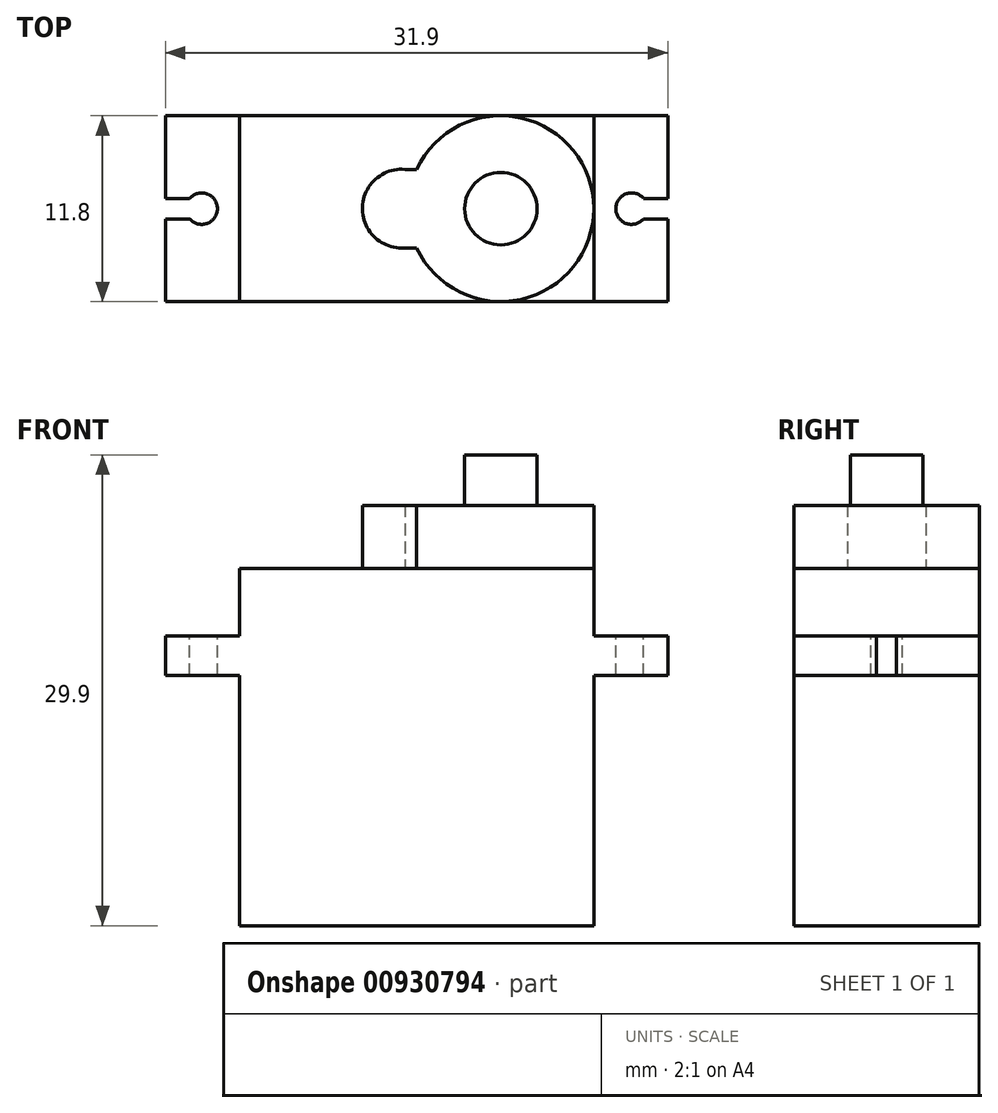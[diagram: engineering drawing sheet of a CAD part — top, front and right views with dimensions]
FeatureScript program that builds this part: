
annotation { "Feature Type Name" : "Feature", "Feature Type Description" : "" }
export const myFeature = defineFeature(function(context is Context, id is Id, definition is map)
    precondition{}
    {
        {
            var Q0;
            Q0=qCreatedBy(makeId("Top.planeOp"),FACE);
            var sketch = newSketch(context, id + "F0", { "sketchPlane" : qUnion([Q0])});
            skLineSegment(sketch, "E0.bottom", {"start": v(11.25, -5.9) * mm, "end": v(-11.25, -5.9) * mm});
            skLineSegment(sketch, "E0.top", {"start": v(11.25, 5.9) * mm, "end": v(-11.25, 5.9) * mm});
            skLineSegment(sketch, "E0.left", {"start": v(11.25, -5.9) * mm, "end": v(11.25, 5.9) * mm});
            skLineSegment(sketch, "E0.right", {"start": v(-11.25, -5.9) * mm, "end": v(-11.25, 5.9) * mm});
            skPoint(sketch, "E0.middle", {"position": v(0, 0) * mm});
            skSolve(sketch);
        }
        {
            var Q0;
            Q0=makeQuery(id+"F0.imprint","IMPRINT",FACE,{"disambiguationData":[TD([[makeQuery(id+"F0.imprint","IMPRINT",EDGE,{"derivedFrom":sQuery(id+"F0.wireOp",EDGE,"E0.bottom")}),-1.0]])]});
            extrude(context, id + "F1", {"entities" : qUnion([Q0]), "depth" : 22.7 * mm, "offsetDistance" : 25 * mm});
        }
        {
            var Q0;
            Q0=makeQuery(id+"F1.opExtrude","SWEPT_FACE",FACE,{"disambiguationData":[OSD([sQuery(id+"F0.wireOp",EDGE,"E0.right")])]});
            var sketch = newSketch(context, id + "F2", { "sketchPlane" : qUnion([Q0])});
            skLineSegment(sketch, "E1", {"start": v(-5.9, 15.9) * mm, "end": v(5.9, 15.9) * mm});
            skLineSegment(sketch, "E2", {"start": v(-5.9, 18.4) * mm, "end": v(5.9, 18.4) * mm});
            skSolve(sketch);
        }
        {
            var Q0;
            Q0 = qSketchRegion(id + "F2", true);
            var Q1;
            {var subQ0=sQuery(id+"F2.wireOp",EDGE,"E1");Q1=makeQuery(id+"F2.imprint","IMPRINT",FACE,{"disambiguationData":[TD([[makeQuery(id+"F2.imprint","IMPRINT",EDGE,{"derivedFrom":subQ0}),1.0]])]});}
            extrude(context, id + "F3", {"entities" : qUnion([Q0, Q1]), "operationType" : NewBodyOperationType.ADD, "depth" : 4.7 * mm, "offsetDistance" : 25 * mm});
        }
        {
            var Q0;
            Q0=makeQuery(id+"F1.opExtrude","SWEPT_FACE",FACE,{"disambiguationData":[OSD([sQuery(id+"F0.wireOp",EDGE,"E0.left")])]});
            var sketch = newSketch(context, id + "F4", { "sketchPlane" : qUnion([Q0])});
            skLineSegment(sketch, "E3", {"start": v(-5.9, 15.9) * mm, "end": v(5.9, 15.9) * mm});
            skLineSegment(sketch, "E4", {"start": v(-5.9, 18.4) * mm, "end": v(5.9, 18.4) * mm});
            skSolve(sketch);
        }
        {
            var Q0;
            Q0 = qSketchRegion(id + "F4", true);
            var Q1;
            {var subQ0=sQuery(id+"F4.wireOp",EDGE,"E3");Q1=makeQuery(id+"F4.imprint","IMPRINT",FACE,{"disambiguationData":[TD([[makeQuery(id+"F4.imprint","IMPRINT",EDGE,{"derivedFrom":subQ0}),1.0]])]});}
            extrude(context, id + "F5", {"entities" : qUnion([Q0, Q1]), "operationType" : NewBodyOperationType.ADD, "depth" : 4.7 * mm, "offsetDistance" : 25 * mm});
        }
        {
            var Q0;
            Q0=makeQuery(id+"F3.opExtrude","SWEPT_FACE",FACE,{"disambiguationData":[OSD([sQuery(id+"F2.wireOp",EDGE,"E2")])]});
            var sketch = newSketch(context, id + "F6", { "sketchPlane" : qUnion([Q0])});
            skLineSegment(sketch, "E5", {"start": v(-15.95, 0) * mm, "end": v(-13.65, 0) * mm});
            skCircle(sketch, "E6", {"center": v(-13.65, 0) * mm, "radius": 1 * mm});
            skLineSegment(sketch, "E7", {"start": v(-15.95, 0.65) * mm, "end": v(-14.4, 0.65) * mm});
            skLineSegment(sketch, "E8", {"start": v(-15.95, -0.65) * mm, "end": v(-14.4, -0.65) * mm});
            skSolve(sketch);
        }
        {
            var Q0;
            {var subQ5=sQuery(id+"F6.wireOp",EDGE,"E7");Q0=makeQuery(id+"F6.imprint","IMPRINT",FACE,{"disambiguationData":[TD([[makeQuery(id+"F6.imprint","IMPRINT",EDGE,{"derivedFrom":subQ5}),-1.0]])]});}
            var Q1;
            {var subQ5=sQuery(id+"F6.wireOp",EDGE,"E8");Q1=makeQuery(id+"F6.imprint","IMPRINT",FACE,{"disambiguationData":[TD([[makeQuery(id+"F6.imprint","IMPRINT",EDGE,{"derivedFrom":subQ5}),1.0]])]});}
            var Q2;
            {var subQ0=sQuery(id+"F6.wireOp",EDGE,"E6");var subQ1=makeQuery(id+"F6.imprint","INTERSECT",VERTEX,{"derivedFrom":[subQ0,sQuery(id+"F6.wireOp",EDGE,"E7")]});Q2=makeQuery(id+"F6.imprint","IMPRINT",FACE,{"disambiguationData":[TD([[makeQuery(id+"F6.imprint","IMPRINT",EDGE,{"disambiguationData":[TD([[subQ1,-1.0]])],"derivedFrom":subQ0}),1.0]])]});}
            extrude(context, id + "F7", {"entities" : qUnion([Q0, Q1, Q2]), "operationType" : NewBodyOperationType.REMOVE, "oppositeDirection" : true, "depth" : 2.5 * mm, "offsetDistance" : 25 * mm});
        }
        {
            var Q0;
            Q0=makeQuery(id+"F5.opExtrude","SWEPT_FACE",FACE,{"disambiguationData":[OSD([sQuery(id+"F4.wireOp",EDGE,"E4")])]});
            var sketch = newSketch(context, id + "F8", { "sketchPlane" : qUnion([Q0])});
            skLineSegment(sketch, "E9", {"start": v(15.95, 0) * mm, "end": v(13.65, 0) * mm});
            skCircle(sketch, "E10", {"center": v(13.65, 0) * mm, "radius": 1 * mm});
            skLineSegment(sketch, "E11", {"start": v(14.4, -0.66) * mm, "end": v(15.95, -0.66) * mm});
            skLineSegment(sketch, "E12", {"start": v(15.95, 0.64) * mm, "end": v(14.42, 0.64) * mm});
            skSolve(sketch);
        }
        {
            var Q0;
            {var subQ5=sQuery(id+"F8.wireOp",EDGE,"E11");Q0=makeQuery(id+"F8.imprint","IMPRINT",FACE,{"disambiguationData":[TD([[makeQuery(id+"F8.imprint","IMPRINT",EDGE,{"derivedFrom":subQ5}),1.0]])]});}
            var Q1;
            {var subQ5=sQuery(id+"F8.wireOp",EDGE,"E12");Q1=makeQuery(id+"F8.imprint","IMPRINT",FACE,{"disambiguationData":[TD([[makeQuery(id+"F8.imprint","IMPRINT",EDGE,{"derivedFrom":subQ5}),1.0]])]});}
            var Q2;
            {var subQ0=sQuery(id+"F8.wireOp",EDGE,"E10");var subQ1=makeQuery(id+"F8.imprint","INTERSECT",VERTEX,{"derivedFrom":[subQ0,sQuery(id+"F8.wireOp",EDGE,"E12")]});Q2=makeQuery(id+"F8.imprint","IMPRINT",FACE,{"disambiguationData":[TD([[makeQuery(id+"F8.imprint","IMPRINT",EDGE,{"disambiguationData":[TD([[subQ1,1.0]])],"derivedFrom":subQ0}),1.0]])]});}
            extrude(context, id + "F9", {"entities" : qUnion([Q0, Q1, Q2]), "operationType" : NewBodyOperationType.REMOVE, "oppositeDirection" : true, "depth" : 2.5 * mm, "offsetDistance" : 25 * mm});
        }
        {
            var Q0;
            Q0=makeQuery(id+"F1.opExtrude","CAP_FACE",FACE,{"disambiguationData":[OSD([sQuery(id+"F0.wireOp",EDGE,"E0.bottom"),sQuery(id+"F0.wireOp",EDGE,"E0.top"),sQuery(id+"F0.wireOp",EDGE,"E0.left"),sQuery(id+"F0.wireOp",EDGE,"E0.right")])],"isStart":false});
            var sketch = newSketch(context, id + "F10", { "sketchPlane" : qUnion([Q0])});
            skCircle(sketch, "E13", {"center": v(5.35, 0) * mm, "radius": 5.9 * mm});
            skCircle(sketch, "E14", {"center": v(-0.95, 0) * mm, "radius": 2.5 * mm});
            skLineSegment(sketch, "E15", {"start": v(-0.95, -2.5) * mm, "end": v(0, -2.5) * mm});
            skLineSegment(sketch, "E16", {"start": v(-1.16, 2.5) * mm, "end": v(0, 2.5) * mm});
            skCircle(sketch, "E17", {"center": v(5.35, 0) * mm, "radius": 2.3 * mm});
            skSolve(sketch);
        }
        {
            var Q0;
            Q0 = qSketchRegion(id + "F10", true);
            var Q1;
            {var subQ0=sQuery(id+"F10.wireOp",EDGE,"E13");var subQ6=makeQuery(id+"F10.imprint","INTERSECT",VERTEX,{"derivedFrom":[makeQuery(id+"F1.opExtrude","CAP_EDGE",EDGE,{"disambiguationData":[OSD([sQuery(id+"F0.wireOp",EDGE,"E0.top")])],"isStart":false}),subQ0]});Q1=makeQuery(id+"F10.imprint","IMPRINT",FACE,{"disambiguationData":[TD([[makeQuery(id+"F10.imprint","IMPRINT",EDGE,{"disambiguationData":[TD([[subQ6,1.0]])],"derivedFrom":subQ0}),1.0]])]});}
            var Q2;
            {var subQ0=sQuery(id+"F10.wireOp",EDGE,"E14");var subQ1=sQuery(id+"F10.wireOp",EDGE,"E13");var subQ2=makeQuery(id+"F10.imprint","INTERSECT",VERTEX,{"disambiguationData":[OD(0.0)],"derivedFrom":[subQ1,subQ0]});Q2=makeQuery(id+"F10.imprint","IMPRINT",FACE,{"disambiguationData":[TD([[makeQuery(id+"F10.imprint","IMPRINT",EDGE,{"disambiguationData":[TD([[subQ2,-1.0]])],"derivedFrom":subQ1}),1.0]])]});}
            extrude(context, id + "F11", {"entities" : qUnion([Q0, Q1, Q2]), "operationType" : NewBodyOperationType.ADD, "depth" : 4 * mm, "offsetDistance" : 25 * mm});
        }
        {
            var Q0;
            Q0=makeQuery(id+"F11.boolean.opBoolean","SPLIT",FACE,{"disambiguationData":[TD([makeQuery(id+"F11.opExtrude","SWEPT_FACE",FACE,{"disambiguationData":[OSD([sQuery(id+"F10.wireOp",EDGE,"E17")])]})])],"derivedFrom":makeQuery(id+"F1.opExtrude","CAP_FACE",FACE,{"disambiguationData":[OSD([sQuery(id+"F0.wireOp",EDGE,"E0.bottom"),sQuery(id+"F0.wireOp",EDGE,"E0.top"),sQuery(id+"F0.wireOp",EDGE,"E0.left"),sQuery(id+"F0.wireOp",EDGE,"E0.right")])],"isStart":false})});
            extrude(context, id + "F12", {"entities" : qUnion([Q0]), "operationType" : NewBodyOperationType.ADD, "depth" : 7.2 * mm, "offsetDistance" : 25 * mm});
        }
    });
